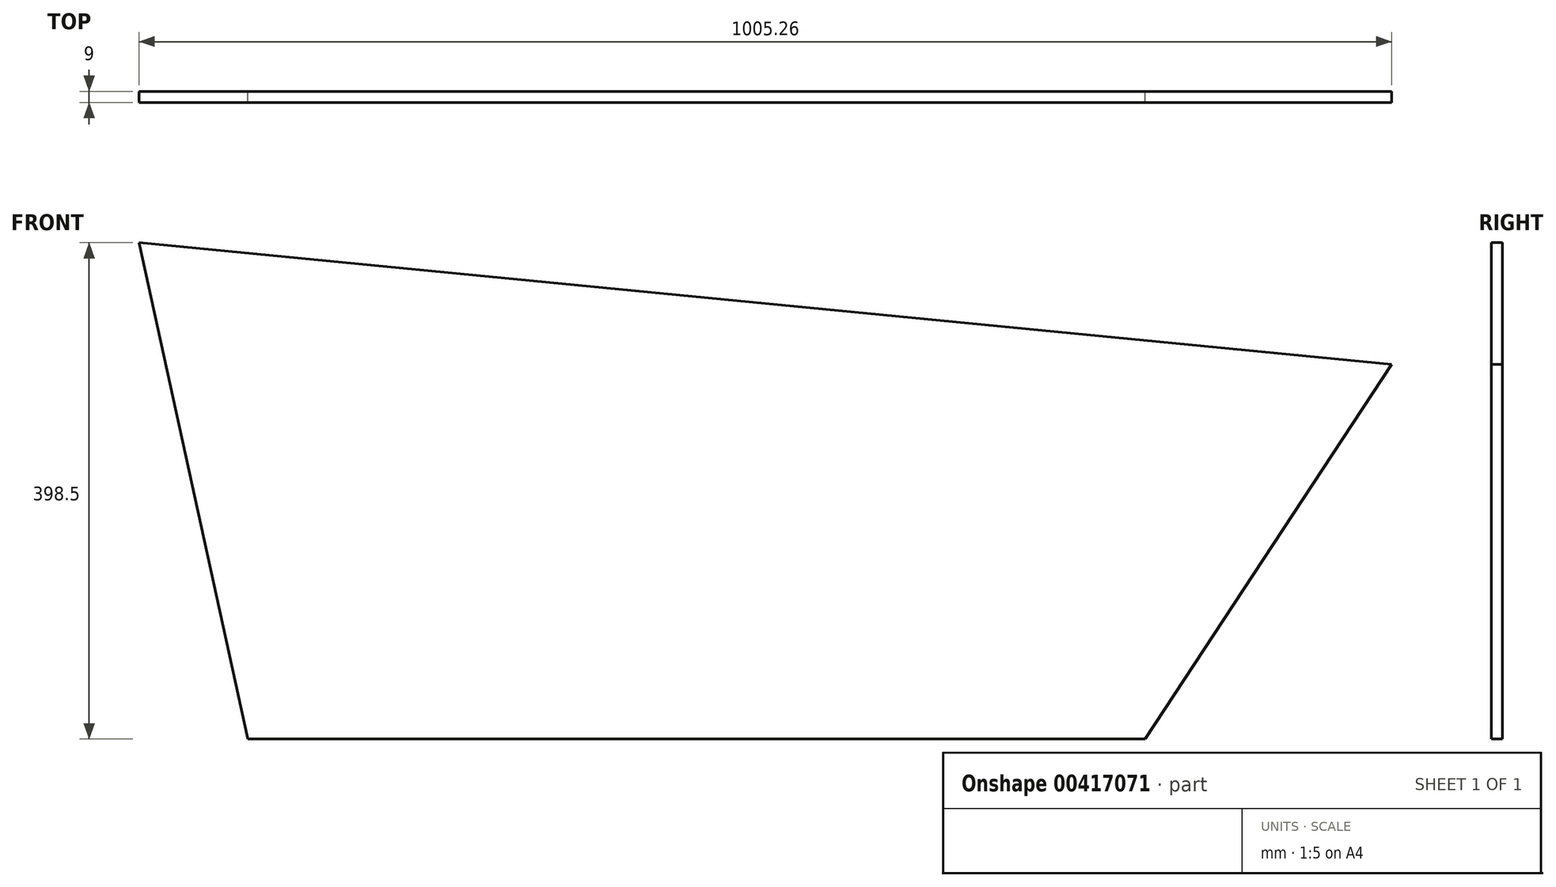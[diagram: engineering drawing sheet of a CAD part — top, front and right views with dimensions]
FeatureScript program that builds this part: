
annotation { "Feature Type Name" : "Feature", "Feature Type Description" : "" }
export const myFeature = defineFeature(function(context is Context, id is Id, definition is map)
    precondition{}
    {
        {
            var Q0;
            Q0=qCreatedBy(makeId("Front.planeOp"),FACE);
            var sketch = newSketch(context, id + "F0", { "sketchPlane" : qUnion([Q0])});
            skLineSegment(sketch, "E0", {"start": v(0, 0) * mm, "end": v(720, 0) * mm});
            skLineSegment(sketch, "E1", {"start": v(720, 0) * mm, "end": v(917.84, 300.77) * mm});
            skLineSegment(sketch, "E2", {"start": v(917.84, 300.77) * mm, "end": v(-87.42, 398.5) * mm});
            skLineSegment(sketch, "E3", {"start": v(-87.42, 398.5) * mm, "end": v(0, 0) * mm});
            skLineSegment(sketch, "E4", {"start": v(0, 0) * mm, "end": v(0, 390) * mm});
            skLineSegment(sketch, "E5", {"start": v(720, 0) * mm, "end": v(720, 320) * mm});
            skSolve(sketch);
        }
        {
            var Q0;
            Q0 = qSketchRegion(id + "F0", true);
            extrude(context, id + "F1", {"entities" : qUnion([Q0]), "depth" : 9 * mm});
        }
    });
